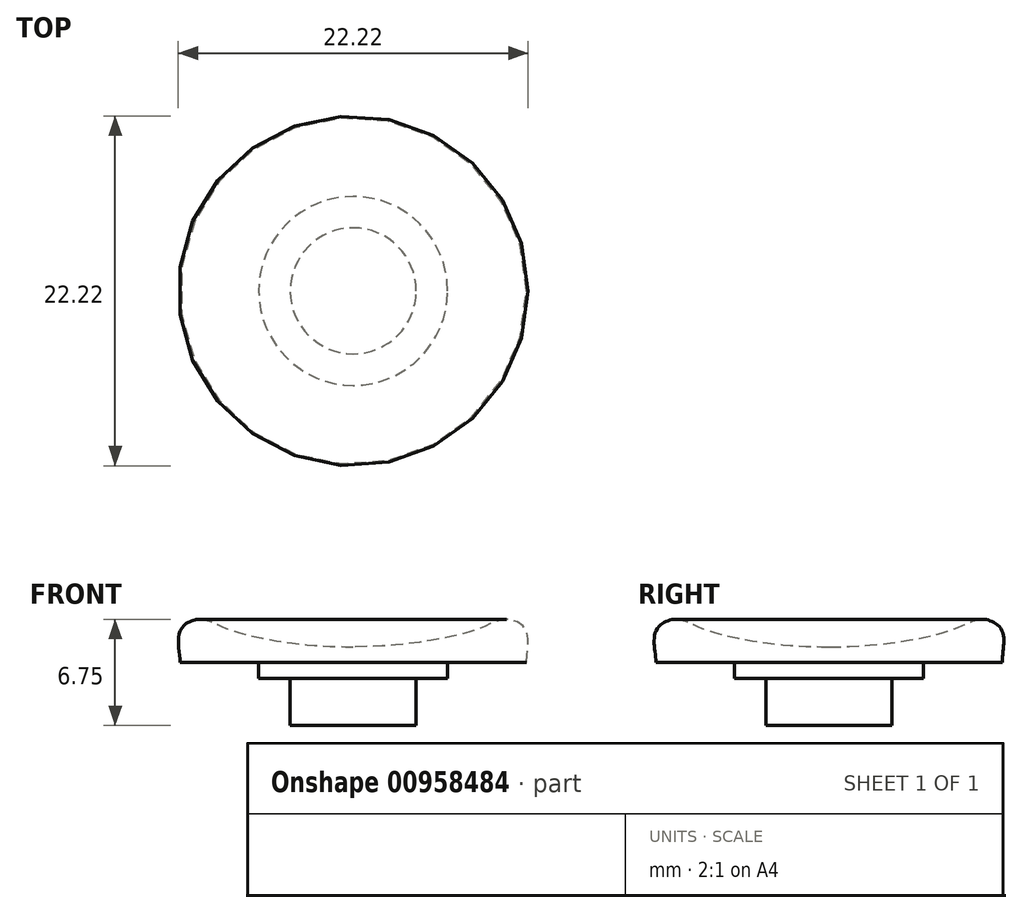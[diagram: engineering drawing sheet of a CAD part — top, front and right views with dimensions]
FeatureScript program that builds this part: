
annotation { "Feature Type Name" : "Feature", "Feature Type Description" : "" }
export const myFeature = defineFeature(function(context is Context, id is Id, definition is map)
    precondition{}
    {
        {
            var Q0;
            Q0=qCreatedBy(makeId("Top.planeOp"),FACE);
            var sketch = newSketch(context, id + "F0", { "sketchPlane" : qUnion([Q0])});
            skCircle(sketch, "E0", {"center": v(0, 0) * mm, "radius": 4 * mm});
            skSolve(sketch);
        }
        {
            var Q0;
            Q0=makeQuery(id+"F0.imprint","IMPRINT",FACE,{"disambiguationData":[TD([[makeQuery(id+"F0.imprint","IMPRINT",EDGE,{"derivedFrom":sQuery(id+"F0.wireOp",EDGE,"E0")}),1.0]])]});
            extrude(context, id + "F1", {"entities" : qUnion([Q0]), "oppositeDirection" : true, "depth" : 3 * mm, "offsetDistance" : 25 * mm});
        }
        {
            var Q0;
            Q0=makeQuery(id+"F1.opExtrude","CAP_FACE",FACE,{"disambiguationData":[OSD([sQuery(id+"F0.wireOp",EDGE,"E0")])],"isStart":true});
            var sketch = newSketch(context, id + "F2", { "sketchPlane" : qUnion([Q0])});
            skCircle(sketch, "E1", {"center": v(0, 0) * mm, "radius": 6 * mm});
            skSolve(sketch);
        }
        {
            var Q0;
            Q0=makeQuery(id+"F2.imprint","IMPRINT",FACE,{"disambiguationData":[TD([[makeQuery(id+"F2.imprint","IMPRINT",EDGE,{"derivedFrom":sQuery(id+"F2.wireOp",EDGE,"E1")}),1.0]])]});
            extrude(context, id + "F3", {"entities" : qUnion([Q0]), "operationType" : NewBodyOperationType.ADD, "depth" : 1 * mm, "offsetDistance" : 25 * mm});
        }
        {
            var Q0;
            Q0=makeQuery(id+"F1.opExtrude","CAP_FACE",FACE,{"disambiguationData":[OSD([sQuery(id+"F0.wireOp",EDGE,"E0")])],"isStart":true});
            var Q1;
            Q1=makeQuery(id+"F3.opExtrude","CAP_FACE",FACE,{"disambiguationData":[OSD([sQuery(id+"F0.wireOp",EDGE,"E0"),sQuery(id+"F2.wireOp",EDGE,"E1")])],"isStart":false});
            extrude(context, id + "F4", {"entities" : qUnion([Q0]), "operationType" : NewBodyOperationType.ADD, "endBound" : BoundingType.UP_TO_SURFACE, "depth" : 25 * mm, "endBoundEntityFace" : qUnion([Q1]), "offsetDistance" : 25 * mm});
        }
        {
            var Q0;
            Q0=qCreatedBy(makeId("Front.planeOp"),FACE);
            var sketch = newSketch(context, id + "F5", { "sketchPlane" : qUnion([Q0])});
            skLineSegment(sketch, "E2.0", {"start": v(-6, 1) * mm, "end": v(6, 1) * mm});
            skLineSegment(sketch, "E3", {"start": v(-6, 0) * mm, "end": v(-6, 0.75) * mm});
            skLineSegment(sketch, "E4", {"start": v(6, 0.75) * mm, "end": v(6, 0) * mm});
            skLineSegment(sketch, "E5.0", {"start": v(-6, 0) * mm, "end": v(6, 0) * mm});
            skLineSegment(sketch, "E6", {"start": v(0, 1) * mm, "end": v(11, 1) * mm});
            skLineSegment(sketch, "E7", {"start": v(0, 1) * mm, "end": v(0, 2) * mm});
            skFitSpline(sketch, "E8", {"points": [v(11, 1) * mm, v(11, 3) * mm, v(9.75, 3.75) * mm, v(8.25, 3.25) * mm, v(5.5, 2.5) * mm, v(0, 2) * mm], "startDerivative": vector(0, 10.92) * mm, "endDerivative": vector(-22.24, 0) * mm});
            skLineSegment(sketch, "E9", {"start": v(0, 2) * mm, "end": v(6.7, 2) * mm, "construction": true});
            skLineSegment(sketch, "E10", {"start": v(11, 1) * mm, "end": v(11, 6) * mm, "construction": true});
            skPoint(sketch, "E11", {"position": v(3.35, 2) * mm});
            skSolve(sketch);
        }
        {
            var Q0;
            {var subQ0=sQuery(id+"F5.wireOp",EDGE,"E7");Q0=makeQuery(id+"F5.imprint","IMPRINT",FACE,{"disambiguationData":[TD([[makeQuery(id+"F5.imprint","IMPRINT",EDGE,{"derivedFrom":subQ0}),-1.0]])]});}
            var Q1;
            Q1=sQuery(id+"F5.wireOp",EDGE,"E7");
            revolve(context, id + "F6", {"operationType" : NewBodyOperationType.ADD, "surfaceOperationType" : NewSurfaceOperationType.NEW, "entities" : qUnion([Q0]), "axis" : qUnion([Q1]), "revolveType" : RevolveType.FULL});
        }
    });
